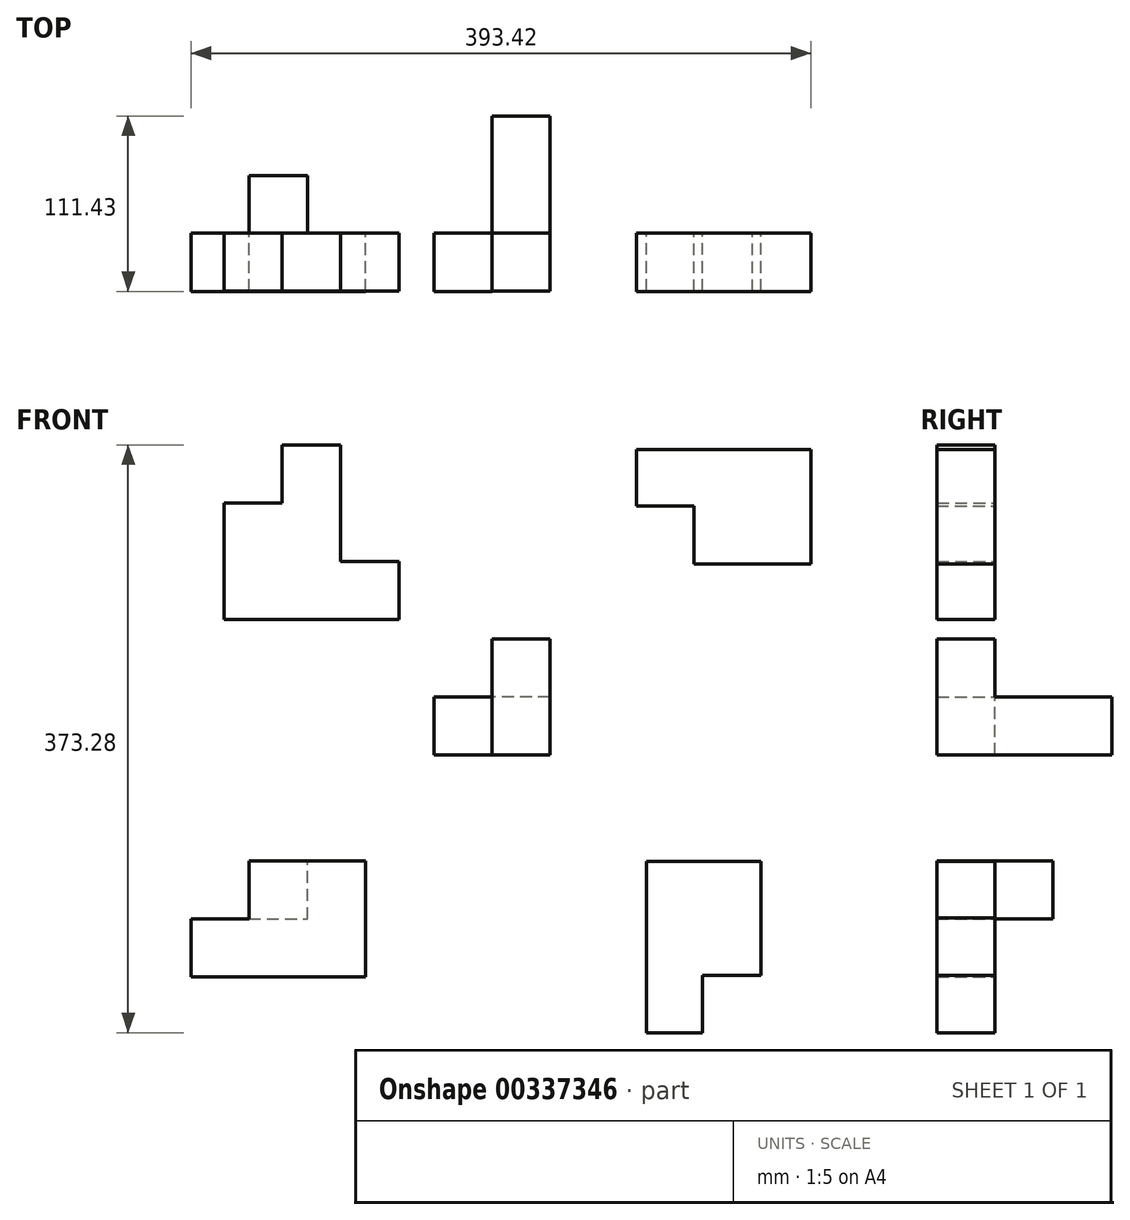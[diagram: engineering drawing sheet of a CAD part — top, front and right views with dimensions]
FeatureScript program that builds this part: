
annotation { "Feature Type Name" : "Feature", "Feature Type Description" : "" }
export const myFeature = defineFeature(function(context is Context, id is Id, definition is map)
    precondition{}
    {
        {
            var Q0;
            Q0=qCreatedBy(makeId("Right.planeOp"),FACE);
            var sketch = newSketch(context, id + "F0", { "sketchPlane" : qUnion([Q0])});
            skLineSegment(sketch, "E0.bottom", {"start": v(-36.87, 37.05) * mm, "end": v(0, 37.05) * mm});
            skLineSegment(sketch, "E0.top", {"start": v(-36.87, 0) * mm, "end": v(0, 0) * mm});
            skLineSegment(sketch, "E0.left", {"start": v(-36.87, 37.05) * mm, "end": v(-36.87, 0) * mm});
            skLineSegment(sketch, "E0.right", {"start": v(0, 37.05) * mm, "end": v(0, 0) * mm});
            skLineSegment(sketch, "E1.top", {"start": v(-36.87, -36.75) * mm, "end": v(0, -36.75) * mm});
            skLineSegment(sketch, "E1.left", {"start": v(-36.87, 0) * mm, "end": v(-36.87, -36.75) * mm});
            skLineSegment(sketch, "E1.right", {"start": v(0, 0) * mm, "end": v(0, -36.75) * mm});
            skLineSegment(sketch, "E2.bottom", {"start": v(0, 0) * mm, "end": v(37.45, 0) * mm});
            skLineSegment(sketch, "E2.top", {"start": v(0, -36.75) * mm, "end": v(37.45, -36.75) * mm});
            skLineSegment(sketch, "E2.right", {"start": v(37.45, 0) * mm, "end": v(37.45, -36.75) * mm});
            skLineSegment(sketch, "E3.left", {"start": v(37.45, 0) * mm, "end": v(37.45, -37.35) * mm});
            skLineSegment(sketch, "E4.bottom", {"start": v(37.45, 0) * mm, "end": v(74.3, 0) * mm});
            skLineSegment(sketch, "E4.top", {"start": v(37.45, -36.75) * mm, "end": v(74.3, -36.75) * mm});
            skLineSegment(sketch, "E4.right", {"start": v(74.3, 0) * mm, "end": v(74.3, -36.75) * mm});
            skSolve(sketch);
        }
        {
            var Q0;
            Q0 = qSketchRegion(id + "F0", true);
            extrude(context, id + "F1", {"entities" : qUnion([Q0]), "depth" : 36.83 * mm, "offsetDistance" : 25.4 * mm});
        }
        {
            var Q0;
            Q0=qCreatedBy(makeId("Top.planeOp"),FACE);
            var sketch = newSketch(context, id + "F2", { "sketchPlane" : qUnion([Q0])});
            skLineSegment(sketch, "E5.bottom", {"start": v(0, -37.13) * mm, "end": v(-36.73, -37.13) * mm});
            skLineSegment(sketch, "E5.top", {"start": v(0, 0) * mm, "end": v(-36.73, 0) * mm});
            skLineSegment(sketch, "E5.left", {"start": v(0, -37.13) * mm, "end": v(0, 0) * mm});
            skLineSegment(sketch, "E5.right", {"start": v(-36.73, -37.13) * mm, "end": v(-36.73, 0) * mm});
            skSolve(sketch);
        }
        {
            var Q0;
            Q0 = qSketchRegion(id + "F2", true);
            extrude(context, id + "F3", {"entities" : qUnion([Q0]), "operationType" : NewBodyOperationType.ADD, "oppositeDirection" : true, "depth" : 36.83 * mm, "offsetDistance" : 25.4 * mm});
        }
        {
            var Q0;
            Q0=qCreatedBy(makeId("Front.planeOp"),FACE);
            var sketch = newSketch(context, id + "F4", { "sketchPlane" : qUnion([Q0])});
            skLineSegment(sketch, "E6.bottom", {"start": v(91.75, 157.34) * mm, "end": v(128.12, 157.34) * mm});
            skLineSegment(sketch, "E6.top", {"start": v(91.75, 121.2) * mm, "end": v(128.12, 121.2) * mm});
            skLineSegment(sketch, "E6.left", {"start": v(91.75, 157.34) * mm, "end": v(91.75, 121.2) * mm});
            skLineSegment(sketch, "E6.right", {"start": v(128.12, 157.34) * mm, "end": v(128.12, 121.2) * mm});
            skLineSegment(sketch, "E7.bottom", {"start": v(128.12, 157.34) * mm, "end": v(165.46, 157.34) * mm});
            skLineSegment(sketch, "E7.top", {"start": v(128.12, 121.2) * mm, "end": v(165.46, 121.2) * mm});
            skLineSegment(sketch, "E7.right", {"start": v(165.46, 157.34) * mm, "end": v(165.46, 121.2) * mm});
            skLineSegment(sketch, "E8.bottom", {"start": v(165.46, 157.34) * mm, "end": v(202.38, 157.34) * mm});
            skLineSegment(sketch, "E8.top", {"start": v(165.46, 121.06) * mm, "end": v(202.38, 121.06) * mm});
            skLineSegment(sketch, "E8.left", {"start": v(165.46, 157.34) * mm, "end": v(165.46, 121.06) * mm});
            skLineSegment(sketch, "E8.right", {"start": v(202.38, 157.34) * mm, "end": v(202.38, 121.06) * mm});
            skLineSegment(sketch, "E9.top", {"start": v(128.12, 84.38) * mm, "end": v(165.46, 84.38) * mm});
            skLineSegment(sketch, "E9.left", {"start": v(128.12, 121.2) * mm, "end": v(128.12, 84.38) * mm});
            skLineSegment(sketch, "E9.right", {"start": v(165.46, 121.2) * mm, "end": v(165.46, 84.38) * mm});
            skLineSegment(sketch, "E10.bottom", {"start": v(165.46, 121.2) * mm, "end": v(202.38, 121.2) * mm});
            skLineSegment(sketch, "E10.top", {"start": v(165.46, 84.39) * mm, "end": v(202.38, 84.39) * mm});
            skLineSegment(sketch, "E10.left", {"start": v(165.46, 121.2) * mm, "end": v(165.46, 84.39) * mm});
            skLineSegment(sketch, "E10.right", {"start": v(202.38, 121.2) * mm, "end": v(202.38, 84.39) * mm});
            skSolve(sketch);
        }
        {
            var Q0;
            Q0 = qSketchRegion(id + "F4", true);
            extrude(context, id + "F5", {"entities" : qUnion([Q0]), "depth" : 37.08 * mm, "offsetDistance" : 25.4 * mm});
        }
        {
            var Q0;
            Q0=qCreatedBy(makeId("Front.planeOp"),FACE);
            var sketch = newSketch(context, id + "F6", { "sketchPlane" : qUnion([Q0])});
            skLineSegment(sketch, "E11.bottom", {"start": v(170.61, -104.28) * mm, "end": v(133.77, -104.28) * mm});
            skLineSegment(sketch, "E11.top", {"start": v(170.61, -140.35) * mm, "end": v(133.77, -140.35) * mm});
            skLineSegment(sketch, "E11.left", {"start": v(170.61, -104.28) * mm, "end": v(170.61, -140.35) * mm});
            skLineSegment(sketch, "E11.right", {"start": v(133.77, -104.28) * mm, "end": v(133.77, -140.35) * mm});
            skLineSegment(sketch, "E12.bottom", {"start": v(133.77, -104.28) * mm, "end": v(98.07, -104.28) * mm});
            skLineSegment(sketch, "E12.top", {"start": v(133.77, -140.36) * mm, "end": v(98.07, -140.36) * mm});
            skLineSegment(sketch, "E12.left", {"start": v(133.77, -104.28) * mm, "end": v(133.77, -140.36) * mm});
            skLineSegment(sketch, "E12.right", {"start": v(98.07, -104.28) * mm, "end": v(98.07, -140.36) * mm});
            skLineSegment(sketch, "E13.bottom", {"start": v(133.77, -140.35) * mm, "end": v(170.73, -140.35) * mm});
            skLineSegment(sketch, "E13.top", {"start": v(133.77, -176.7) * mm, "end": v(170.73, -176.7) * mm});
            skLineSegment(sketch, "E13.left", {"start": v(133.77, -140.35) * mm, "end": v(133.77, -176.7) * mm});
            skLineSegment(sketch, "E13.right", {"start": v(170.73, -140.35) * mm, "end": v(170.73, -176.7) * mm});
            skLineSegment(sketch, "E14.bottom", {"start": v(133.77, -176.7) * mm, "end": v(98.07, -176.7) * mm});
            skLineSegment(sketch, "E14.left", {"start": v(133.77, -176.7) * mm, "end": v(133.77, -140.36) * mm});
            skLineSegment(sketch, "E14.right", {"start": v(98.07, -176.7) * mm, "end": v(98.07, -140.36) * mm});
            skLineSegment(sketch, "E15.top", {"start": v(133.77, -213.18) * mm, "end": v(98.07, -213.18) * mm});
            skLineSegment(sketch, "E15.left", {"start": v(133.77, -176.7) * mm, "end": v(133.77, -213.18) * mm});
            skLineSegment(sketch, "E15.right", {"start": v(98.07, -176.7) * mm, "end": v(98.07, -213.18) * mm});
            skSolve(sketch);
        }
        {
            var Q0;
            Q0 = qSketchRegion(id + "F6", true);
            extrude(context, id + "F7", {"entities" : qUnion([Q0]), "depth" : 36.83 * mm, "offsetDistance" : 25.4 * mm});
        }
        {
            var Q0;
            Q0=qCreatedBy(makeId("Front.planeOp"),FACE);
            var sketch = newSketch(context, id + "F8", { "sketchPlane" : qUnion([Q0])});
            skLineSegment(sketch, "E16.bottom", {"start": v(-133.32, 49.17) * mm, "end": v(-96.27, 49.17) * mm});
            skLineSegment(sketch, "E16.top", {"start": v(-133.32, 86.07) * mm, "end": v(-96.27, 86.07) * mm});
            skLineSegment(sketch, "E16.left", {"start": v(-133.32, 49.17) * mm, "end": v(-133.32, 86.07) * mm});
            skLineSegment(sketch, "E16.right", {"start": v(-96.27, 49.17) * mm, "end": v(-96.27, 86.07) * mm});
            skLineSegment(sketch, "E17.top", {"start": v(-133.32, 123.12) * mm, "end": v(-96.27, 123.12) * mm});
            skLineSegment(sketch, "E17.left", {"start": v(-133.32, 86.07) * mm, "end": v(-133.32, 123.12) * mm});
            skLineSegment(sketch, "E17.right", {"start": v(-96.27, 86.07) * mm, "end": v(-96.27, 123.12) * mm});
            skLineSegment(sketch, "E18.top", {"start": v(-133.32, 160.1) * mm, "end": v(-96.27, 160.1) * mm});
            skLineSegment(sketch, "E18.left", {"start": v(-133.32, 123.12) * mm, "end": v(-133.32, 160.1) * mm});
            skLineSegment(sketch, "E18.right", {"start": v(-96.27, 123.12) * mm, "end": v(-96.27, 160.1) * mm});
            skLineSegment(sketch, "E19.bottom", {"start": v(-133.32, 49.17) * mm, "end": v(-170.32, 49.17) * mm});
            skLineSegment(sketch, "E19.top", {"start": v(-133.32, 86.07) * mm, "end": v(-170.32, 86.07) * mm});
            skLineSegment(sketch, "E19.right", {"start": v(-170.32, 49.17) * mm, "end": v(-170.32, 86.07) * mm});
            skLineSegment(sketch, "E20.bottom", {"start": v(-170.32, 86.07) * mm, "end": v(-133.32, 86.07) * mm});
            skLineSegment(sketch, "E20.top", {"start": v(-170.32, 123.12) * mm, "end": v(-133.32, 123.12) * mm});
            skLineSegment(sketch, "E20.left", {"start": v(-170.32, 86.07) * mm, "end": v(-170.32, 123.12) * mm});
            skLineSegment(sketch, "E21.bottom", {"start": v(-96.27, 49.17) * mm, "end": v(-59.04, 49.17) * mm});
            skLineSegment(sketch, "E21.top", {"start": v(-96.27, 86.07) * mm, "end": v(-59.04, 86.07) * mm});
            skLineSegment(sketch, "E21.right", {"start": v(-59.04, 49.17) * mm, "end": v(-59.04, 86.07) * mm});
            skSolve(sketch);
        }
        {
            var Q0;
            Q0 = qSketchRegion(id + "F8", true);
            extrude(context, id + "F9", {"entities" : qUnion([Q0]), "depth" : 36.83 * mm, "offsetDistance" : 25.4 * mm});
        }
        {
            var Q0;
            Q0=qCreatedBy(makeId("Front.planeOp"),FACE);
            var sketch = newSketch(context, id + "F10", { "sketchPlane" : qUnion([Q0])});
            skLineSegment(sketch, "E22.bottom", {"start": v(-154.46, -177.64) * mm, "end": v(-117.25, -177.64) * mm});
            skLineSegment(sketch, "E22.top", {"start": v(-154.46, -140.98) * mm, "end": v(-117.25, -140.98) * mm});
            skLineSegment(sketch, "E22.left", {"start": v(-154.46, -177.64) * mm, "end": v(-154.46, -140.98) * mm});
            skLineSegment(sketch, "E22.right", {"start": v(-117.25, -177.64) * mm, "end": v(-117.25, -140.98) * mm});
            skLineSegment(sketch, "E23.bottom", {"start": v(-117.25, -177.64) * mm, "end": v(-80.3, -177.64) * mm});
            skLineSegment(sketch, "E23.top", {"start": v(-117.25, -140.98) * mm, "end": v(-80.3, -140.98) * mm});
            skLineSegment(sketch, "E23.right", {"start": v(-80.3, -177.64) * mm, "end": v(-80.3, -140.98) * mm});
            skLineSegment(sketch, "E24.bottom", {"start": v(-117.25, -140.98) * mm, "end": v(-154.46, -140.98) * mm});
            skLineSegment(sketch, "E24.top", {"start": v(-117.25, -104.04) * mm, "end": v(-154.46, -104.04) * mm});
            skLineSegment(sketch, "E24.left", {"start": v(-117.25, -140.98) * mm, "end": v(-117.25, -104.04) * mm});
            skLineSegment(sketch, "E24.right", {"start": v(-154.46, -140.98) * mm, "end": v(-154.46, -104.04) * mm});
            skLineSegment(sketch, "E25.top", {"start": v(-117.25, -104.04) * mm, "end": v(-80.3, -104.04) * mm});
            skLineSegment(sketch, "E25.right", {"start": v(-80.3, -140.98) * mm, "end": v(-80.3, -104.04) * mm});
            skLineSegment(sketch, "E26.bottom", {"start": v(-154.46, -140.98) * mm, "end": v(-191.04, -140.98) * mm});
            skLineSegment(sketch, "E26.top", {"start": v(-154.46, -177.64) * mm, "end": v(-191.04, -177.64) * mm});
            skLineSegment(sketch, "E26.left", {"start": v(-154.46, -140.98) * mm, "end": v(-154.46, -177.64) * mm});
            skLineSegment(sketch, "E26.right", {"start": v(-191.04, -140.98) * mm, "end": v(-191.04, -177.64) * mm});
            skSolve(sketch);
        }
        {
            var Q0;
            Q0 = qSketchRegion(id + "F10", true);
            extrude(context, id + "F11", {"entities" : qUnion([Q0]), "depth" : 37.08 * mm, "offsetDistance" : 25.4 * mm});
        }
        {
            var Q0;
            Q0=makeQuery(id+"F10.imprint","IMPRINT",FACE,{"disambiguationData":[TD([[makeQuery(id+"F10.imprint","IMPRINT",EDGE,{"derivedFrom":sQuery(id+"F10.wireOp",EDGE,"E22.top")}),1.0]])]});
            extrude(context, id + "F12", {"entities" : qUnion([Q0]), "operationType" : NewBodyOperationType.ADD, "oppositeDirection" : true, "depth" : 36.58 * mm, "offsetDistance" : 25.4 * mm});
        }
    });
